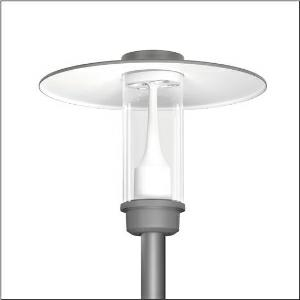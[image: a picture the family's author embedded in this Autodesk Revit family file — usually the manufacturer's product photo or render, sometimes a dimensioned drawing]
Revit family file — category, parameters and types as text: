
# Revit family: litepole_2_iq___st1_2a_5xa5425ef14h_fad6
name_source: partatom
category: Lighting Fixtures
units: mm (PartAtom-declared; Revit-internal decimal feet)

## family parameters
Cut with Voids When Loaded = No
Host = Face
Light Source = No
Part Type = Normal
Room Calculation Point = No
Round Connector Dimension = Use Diameter
Shared = No

## types (1)
- --- (1 x LED, 1550 lm, 10.5 W, 3000K)
    Apparent Load = 11 VA
    CIE Flux Codes = 22 60 92 98 100
    Color Rendering = 70
    Color Temperature = 3000K
    Default Elevation = 1800 mm
    Description = Litepole 2 iQ, mast luminaire, Module 540 iQ-SR, primary light control with 3 zone facetted reflector, of plastic, silver coated, highly specular, structured, primary optical cover: cover, of PMMA, transparent, light distribution: ST1.2a, light emission: direct distribution, primary light characteristic: asymmetric, installation type: post-top, LED, High Power LED, rated luminous flux: 1.550lm, luminous efficacy: 148lm/W, light colour: 730, colour temperature: 3000K, control gear: iQ Street-Remote, control: Auto-Match, Temp-Guard, Lumen-Switch, Night-Set, Smart-Wire, Light-Fading, Desk-Remote (wireless, voltage-free reading and setting of iQ features in the workshop via application-optimized NFC function/RFID function), optimised constant luminous flux control (CLO 2.0), Street-Remote, pre-setting: logarithmic dimming characteristic, with terminal, 6-pole, max. 2.5mm², mains connection: 230..240V, AC, 50/60Hz, start of lifetime: 11W, end of service life: 11W, reduction: 5W, luminaire housing, upper part, of aluminium, coated, Siteco® metallic grey (DB 702S), diameter: 750mm, height: 590mm, spigot size: d x l = 76 x 70mm (post-top) | with reducer (optional accessory) 60 x 70mm, mounting height: 3..5m, post-top mast mounting element, of diecast aluminium, coated, Siteco® metallic grey (DB 702S), Module 540 iQ-SR, traffic white (RAL 9016), equipment: standard, protection rating (complete): IP65, insulation class (complete): insulation class II (safety insulation), certification: CE, ENEC, VDE, packaging unit: 1 piece

Light Distribution: ST1.2a
    Height = 590 mm
    Lamp = 1 x LED
    Lamp Light Flux = 1550 lm
    Lamp Power = 10.5 W
    Lamp count = 1
    Length = 750 mm
    Luminous efficacy = 148 lm/W
    Manufacturer = Siteco
    ModVariant = No
    Model = 5XA5425EF14H
    Number of Poles = 1
    OnlyDefault = Yes
    Power Factor = 1
    Product Name = Litepole 2 iQ | ST1.2a
    Product group = mast luminaire | pylon top
    ProductGroupID = 6100
    Protection Class = Protection class II
    Protection Degree = IP 65
    RLX_Detail_Level = 1
    RLX_Emergency_Light_Flux = 0 lm
    RLX_Emergency_Type = 0
    RLX_Emergency_Type_DB = No
    RlxData = <blob elided: 63385 chars, md5=d4016515>
    Socket = socket
    Standby Power = 0 W
    System Light Flux = 1550 lm
    System Power = 11 W
    Type Comments = factory setting: luminous flux: 100 % | dim-lin: 254 | 419 mA
    Type Image = l_1006518.jpg
    URL = http://relux.com
    VarID = @adj_190107
    Voltage = 0 V
    Weight = 0.00 kg
    Width = 0 mm  [stored 0 ft]

note: [stored X ft] marks values corroborated as IEEE doubles in the binary element streams (Revit-internal decimal feet)

## geometry (parser evidence)
native form markers: Blend x4, Sweep x10
no freeform markers — native parametric forms only
